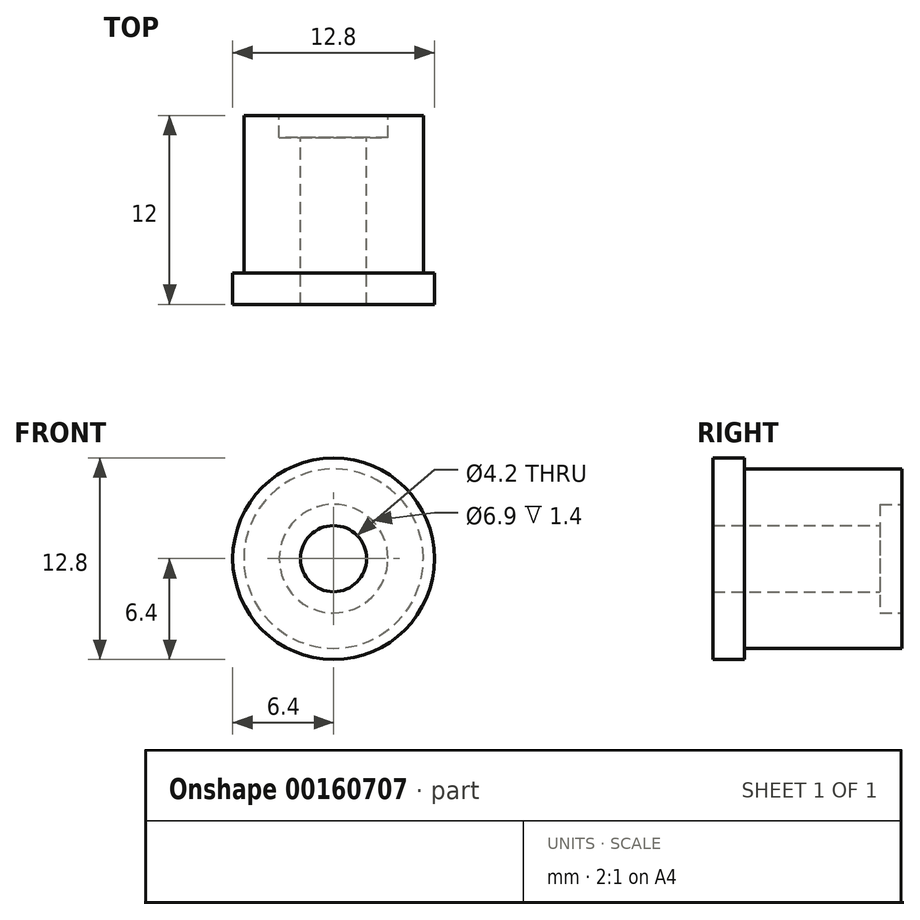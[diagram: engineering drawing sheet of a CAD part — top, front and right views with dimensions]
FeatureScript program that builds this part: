
annotation { "Feature Type Name" : "Feature", "Feature Type Description" : "" }
export const myFeature = defineFeature(function(context is Context, id is Id, definition is map)
    precondition{}
    {
        {
            var Q0;
            Q0=qCreatedBy(makeId("Right.planeOp"),FACE);
            var sketch = newSketch(context, id + "F0", { "sketchPlane" : qUnion([Q0])});
            skLineSegment(sketch, "E0", {"start": v(11.47, 0) * mm, "end": v(0, 0) * mm, "construction": true});
            skLineSegment(sketch, "E1", {"start": v(10.6, 2.1) * mm, "end": v(0, 2.1) * mm});
            skLineSegment(sketch, "E2", {"start": v(10.6, 2.1) * mm, "end": v(10.6, 3.45) * mm});
            skLineSegment(sketch, "E3", {"start": v(12, 3.45) * mm, "end": v(10.6, 3.45) * mm});
            skLineSegment(sketch, "E4", {"start": v(12, 3.45) * mm, "end": v(12, 5.7) * mm});
            skLineSegment(sketch, "E5", {"start": v(2, 5.7) * mm, "end": v(12, 5.7) * mm});
            skLineSegment(sketch, "E6", {"start": v(2, 5.7) * mm, "end": v(2, 6.4) * mm});
            skLineSegment(sketch, "E7", {"start": v(0, 6.4) * mm, "end": v(2, 6.4) * mm});
            skLineSegment(sketch, "E8", {"start": v(0, 6.4) * mm, "end": v(0, 2.1) * mm});
            skSolve(sketch);
        }
        {
            var Q0;
            Q0=makeQuery(id+"F0.imprint","IMPRINT",FACE,{"disambiguationData":[TD([[makeQuery(id+"F0.imprint","IMPRINT",EDGE,{"derivedFrom":sQuery(id+"F0.wireOp",EDGE,"E1")}),-1.0]])]});
            var Q1;
            Q1=sQuery(id+"F0.wireOp",EDGE,"E0");
            revolve(context, id + "F1", {"entities" : qUnion([Q0]), "axis" : qUnion([Q1]), "revolveType" : RevolveType.FULL});
        }
    });
